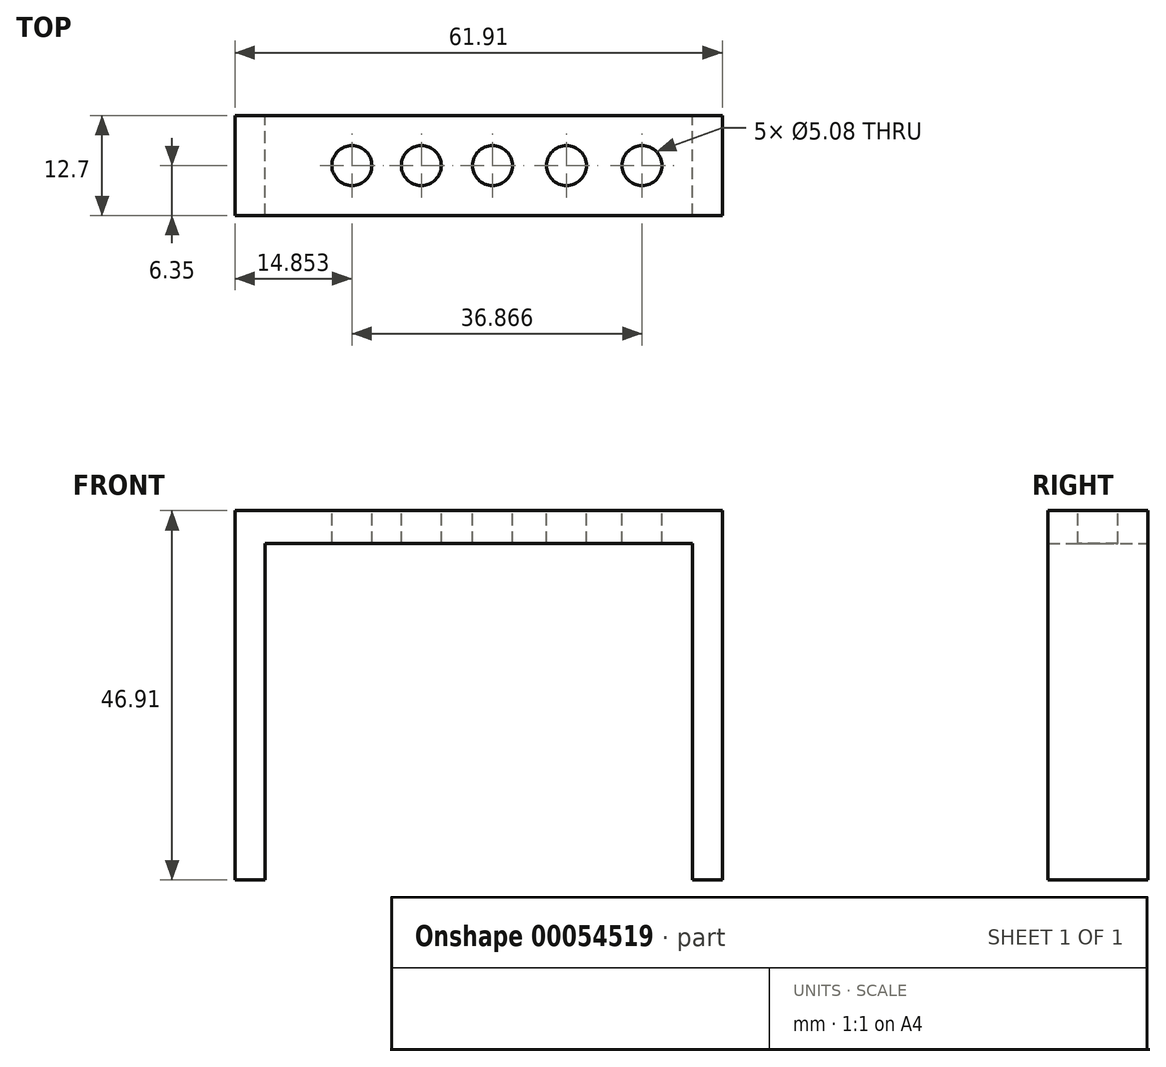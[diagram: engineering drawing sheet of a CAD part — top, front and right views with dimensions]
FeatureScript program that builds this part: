
annotation { "Feature Type Name" : "Feature", "Feature Type Description" : "" }
export const myFeature = defineFeature(function(context is Context, id is Id, definition is map)
    precondition{}
    {
        {
            var Q0;
            Q0=qCreatedBy(makeId("Front.planeOp"),FACE);
            var sketch = newSketch(context, id + "F0", { "sketchPlane" : qUnion([Q0])});
            skLineSegment(sketch, "E0.bottom", {"start": v(-27.74, 0) * mm, "end": v(-31.55, 0) * mm});
            skLineSegment(sketch, "E0.top", {"start": v(-27.74, 42.74) * mm, "end": v(-31.55, 42.74) * mm});
            skLineSegment(sketch, "E0.left", {"start": v(-27.74, 0) * mm, "end": v(-27.74, 42.74) * mm});
            skLineSegment(sketch, "E0.right", {"start": v(-31.55, 0) * mm, "end": v(-31.55, 42.74) * mm});
            skLineSegment(sketch, "E1.bottom", {"start": v(30.36, 0) * mm, "end": v(26.55, 0) * mm});
            skLineSegment(sketch, "E1.top", {"start": v(30.36, 42.74) * mm, "end": v(26.55, 42.74) * mm});
            skLineSegment(sketch, "E1.left", {"start": v(30.36, 0) * mm, "end": v(30.36, 42.74) * mm});
            skLineSegment(sketch, "E1.right", {"start": v(26.55, 0) * mm, "end": v(26.55, 42.74) * mm});
            skLineSegment(sketch, "E2.bottom", {"start": v(-31.55, 42.74) * mm, "end": v(30.36, 42.74) * mm});
            skLineSegment(sketch, "E2.top", {"start": v(-31.55, 46.91) * mm, "end": v(30.36, 46.91) * mm});
            skLineSegment(sketch, "E2.left", {"start": v(-31.55, 42.74) * mm, "end": v(-31.55, 46.91) * mm});
            skLineSegment(sketch, "E2.right", {"start": v(30.36, 42.74) * mm, "end": v(30.36, 46.91) * mm});
            skSolve(sketch);
        }
        {
            var Q0;
            Q0=makeQuery(id+"F0.imprint","IMPRINT",FACE,{"disambiguationData":[TD([[makeQuery(id+"F0.imprint","IMPRINT",EDGE,{"derivedFrom":sQuery(id+"F0.wireOp",EDGE,"E0.bottom")}),-1.0]])]});
            var Q1;
            Q1=makeQuery(id+"F0.imprint","IMPRINT",FACE,{"disambiguationData":[TD([[makeQuery(id+"F0.imprint","IMPRINT",EDGE,{"derivedFrom":sQuery(id+"F0.wireOp",EDGE,"E1.bottom")}),-1.0]])]});
            var Q2;
            Q2=makeQuery(id+"F0.imprint","IMPRINT",FACE,{"disambiguationData":[TD([[makeQuery(id+"F0.imprint","IMPRINT",EDGE,{"derivedFrom":sQuery(id+"F0.wireOp",EDGE,"E2.top")}),-1.0]])]});
            extrude(context, id + "F1", {"entities" : qUnion([Q0, Q1, Q2]), "depth" : 12.7 * mm});
        }
        {
            var Q0;
            Q0=makeQuery(id+"F1.opExtrude","SWEPT_FACE",FACE,{"disambiguationData":[OSD([sQuery(id+"F0.wireOp",EDGE,"E2.top")])]});
            var sketch = newSketch(context, id + "F2", { "sketchPlane" : qUnion([Q0])});
            skCircle(sketch, "E3", {"center": v(-16.7, -6.35) * mm, "radius": 2.54 * mm});
            skPoint(sketch, "E3.centerSnap0", {"position": v(-31.55, -6.35) * mm});
            skCircle(sketch, "E4", {"center": v(-7.88, -6.35) * mm, "radius": 2.54 * mm});
            skCircle(sketch, "E5", {"center": v(10.55, -6.35) * mm, "radius": 2.54 * mm});
            skCircle(sketch, "E6", {"center": v(20.17, -6.35) * mm, "radius": 2.54 * mm});
            skCircle(sketch, "E7", {"center": v(1.15, -6.35) * mm, "radius": 2.54 * mm});
            skSolve(sketch);
        }
        {
            var Q0;
            Q0=makeQuery(id+"F2.imprint","IMPRINT",FACE,{"disambiguationData":[TD([[makeQuery(id+"F2.imprint","IMPRINT",EDGE,{"derivedFrom":sQuery(id+"F2.wireOp",EDGE,"E3")}),1.0]])]});
            var Q1;
            Q1=makeQuery(id+"F2.imprint","IMPRINT",FACE,{"disambiguationData":[TD([[makeQuery(id+"F2.imprint","IMPRINT",EDGE,{"derivedFrom":sQuery(id+"F2.wireOp",EDGE,"E4")}),1.0]])]});
            var Q2;
            Q2=makeQuery(id+"F2.imprint","IMPRINT",FACE,{"disambiguationData":[TD([[makeQuery(id+"F2.imprint","IMPRINT",EDGE,{"derivedFrom":sQuery(id+"F2.wireOp",EDGE,"E7")}),1.0]])]});
            var Q3;
            Q3=makeQuery(id+"F2.imprint","IMPRINT",FACE,{"disambiguationData":[TD([[makeQuery(id+"F2.imprint","IMPRINT",EDGE,{"derivedFrom":sQuery(id+"F2.wireOp",EDGE,"E5")}),1.0]])]});
            var Q4;
            Q4=makeQuery(id+"F2.imprint","IMPRINT",FACE,{"disambiguationData":[TD([[makeQuery(id+"F2.imprint","IMPRINT",EDGE,{"derivedFrom":sQuery(id+"F2.wireOp",EDGE,"E6")}),1.0]])]});
            extrude(context, id + "F3", {"entities" : qUnion([Q0, Q1, Q2, Q3, Q4]), "operationType" : NewBodyOperationType.REMOVE, "oppositeDirection" : true, "depth" : 25.4 * mm});
        }
    });
